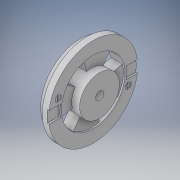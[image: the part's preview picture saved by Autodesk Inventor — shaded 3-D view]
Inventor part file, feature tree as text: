
AUTODESK INVENTOR PART (.ipt)
format: ipt  version: 2016 (Build 200138000, 138)  size: 206,336 bytes
history: native  units: in
note: dims shown in document units (in); Inventor stores cm internally (conversion verified against a paired STEP export)
features: sketch x7, extrude x6, plane x1, loft x1, pattern_circular x1
ambient origin geometry x8: Origin, YZ Plane, XZ Plane, XY Plane, X Axis, Y Axis, Z Axis, Center Point
bodies: Solid1 (feature_tree)
feature tree (16):
  extrude  "Extrusion1"  Depth=0.1in TaperAngle=0.0deg
  sketch  "Sketch2"  dims[d3=1.3in d4=-0.1in]
  plane  "Work Plane1"
  loft  "Loft1"
  extrude  "Extrusion2"  TaperAngle=0.0deg  [1 undecoded]
  sketch  "Sketch5"  dims[d11=0.1in d12=0.0in d13=1.0in]
  extrude  "Extrusion3"  Depth=0.625in
  extrude  "Extrusion4"  Depth=0.1in
  extrude  "Extrusion5"  Depth=0.125in TaperAngle=0.0deg
  extrude  "Extrusion6"  Depth=0.05in
  pattern_circular  "Circular Pattern1"  [2 undecoded]
  sketch  "Sketch1"  dims[d0=1.4in d1=0.1in d2=0.0in]
  sketch  "Sketch3"  dims[d5=1.25in d6=0.0in d7=90.0deg]
  sketch  "Sketch4"  dims[d8=0.0in d9=90.0deg d10=0.625in]
  sketch  "Sketch7"  dims[d14=0.625in d15=0.125in d16=0.0in]
  sketch  "Sketch8"  dims[d17=0.0938in d18=0.0938in d19=1.05in d20=0.125in d21=0.0in d22=0.1in d23=0.1in d24=0.01in d25=0.01in d27=0.01in d28=0.01in d29=0.01in d30=0.005in d31=0.0in d32=0.125in d33=0.2749in d34=0.625in d35=0.05in d36=0.0in d37=1.5748in d38=360.0deg]
note: 3 required parameter values undecoded (feature->parameter linkage not recoverable at this tier; creation-order binding heuristic only, values carry confidence <= 0.55)
